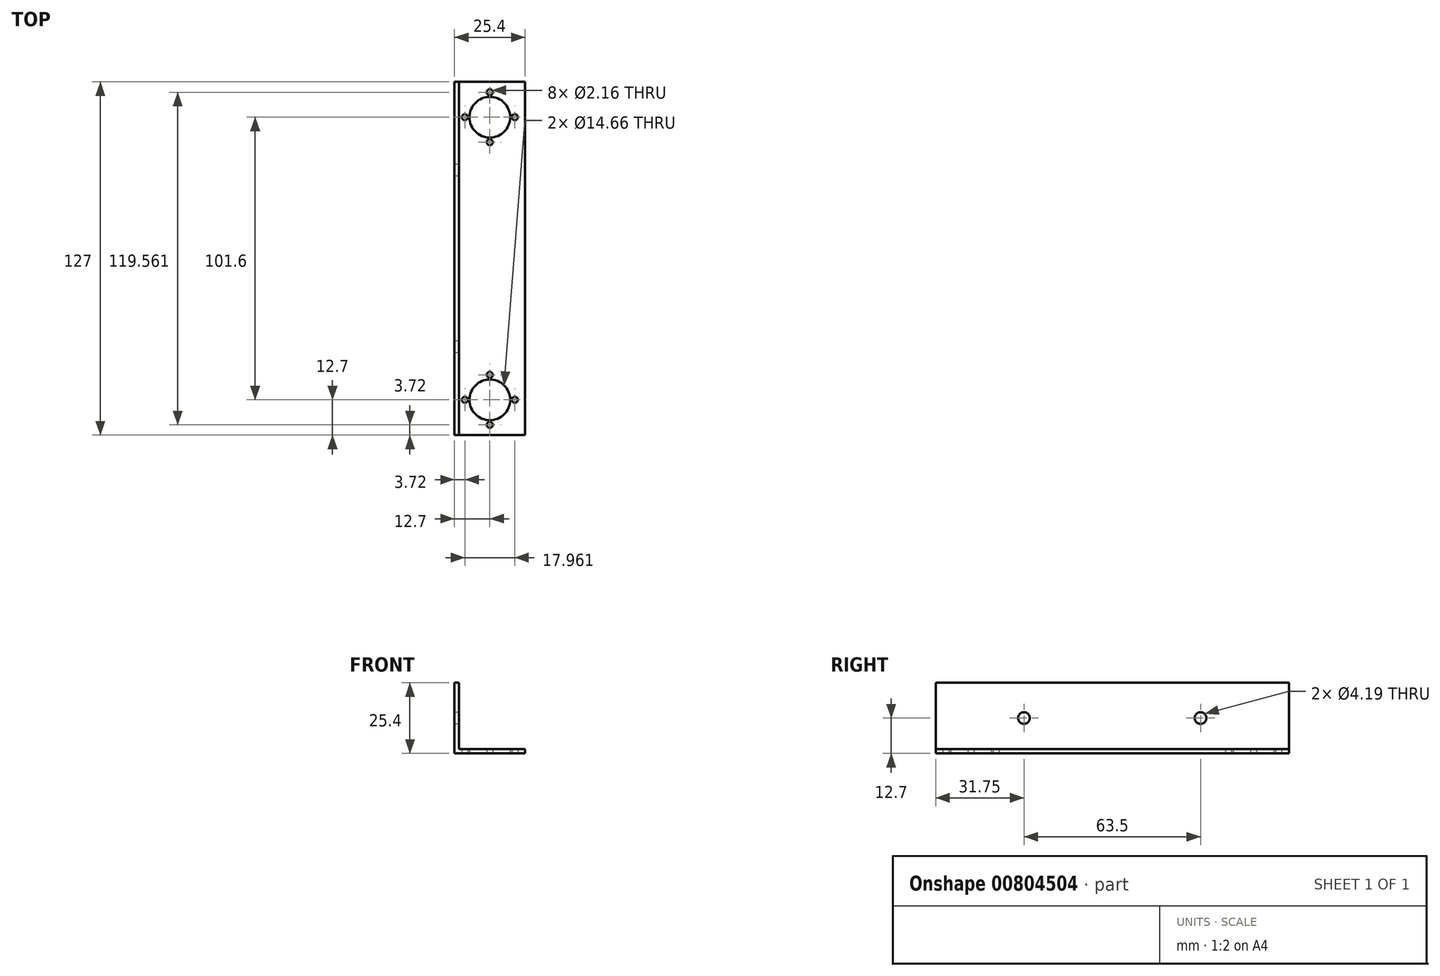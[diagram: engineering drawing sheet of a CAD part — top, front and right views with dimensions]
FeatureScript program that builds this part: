
annotation { "Feature Type Name" : "Feature", "Feature Type Description" : "" }
export const myFeature = defineFeature(function(context is Context, id is Id, definition is map)
    precondition{}
    {
        {
            var Q0;
            Q0=qCreatedBy(makeId("Top.planeOp"),FACE);
            var sketch = newSketch(context, id + "F0", { "sketchPlane" : qUnion([Q0])});
            skLineSegment(sketch, "E0", {"start": v(0, 0) * mm, "end": v(19.87, 0) * mm, "construction": true});
            skCircle(sketch, "E1", {"center": v(0, 50.8) * mm, "radius": 7.33 * mm});
            skLineSegment(sketch, "E2", {"start": v(0, 59.78) * mm, "end": v(0, 41.82) * mm, "construction": true});
            skLineSegment(sketch, "E3", {"start": v(-8.98, 50.8) * mm, "end": v(8.98, 50.8) * mm, "construction": true});
            skCircle(sketch, "E4", {"center": v(0, 59.78) * mm, "radius": 1.08 * mm});
            skCircle(sketch, "E5", {"center": v(8.98, 50.8) * mm, "radius": 1.08 * mm});
            skCircle(sketch, "E6", {"center": v(0, 41.82) * mm, "radius": 1.08 * mm});
            skCircle(sketch, "E7", {"center": v(-8.98, 50.8) * mm, "radius": 1.08 * mm});
            skSolve(sketch);
        }
        {
            var Q0;
            Q0=qCreatedBy(makeId("Front.planeOp"),FACE);
            var sketch = newSketch(context, id + "F1", { "sketchPlane" : qUnion([Q0])});
            skLineSegment(sketch, "E8", {"start": v(12.7, 1.59) * mm, "end": v(-11.11, 1.59) * mm});
            skLineSegment(sketch, "E9", {"start": v(-11.11, 1.59) * mm, "end": v(-11.11, 25.4) * mm});
            skLineSegment(sketch, "E10", {"start": v(-11.11, 25.4) * mm, "end": v(-12.7, 25.4) * mm});
            skLineSegment(sketch, "E11", {"start": v(-12.7, 25.4) * mm, "end": v(-12.7, 0) * mm});
            skLineSegment(sketch, "E12", {"start": v(-12.7, 0) * mm, "end": v(12.7, 0) * mm});
            skLineSegment(sketch, "E13", {"start": v(12.7, 0) * mm, "end": v(12.7, 1.59) * mm});
            skSolve(sketch);
        }
        {
            var Q0;
            Q0=makeQuery(id+"F1.imprint","IMPRINT",FACE,{"disambiguationData":[TD([[makeQuery(id+"F1.imprint","IMPRINT",EDGE,{"derivedFrom":sQuery(id+"F1.wireOp",EDGE,"E8")}),1.0]])]});
            extrude(context, id + "F2", {"entities" : qUnion([Q0]), "endBound" : BoundingType.SYMMETRIC, "depth" : 127 * mm, "offsetDistance" : 25.4 * mm});
        }
        {
            var Q0;
            Q0=makeQuery(id+"F0.imprint","IMPRINT",FACE,{"disambiguationData":[TD([[makeQuery(id+"F0.imprint","IMPRINT",EDGE,{"derivedFrom":sQuery(id+"F0.wireOp",EDGE,"E1")}),1.0]])]});
            var Q1;
            Q1=makeQuery(id+"F0.imprint","IMPRINT",FACE,{"disambiguationData":[TD([[makeQuery(id+"F0.imprint","IMPRINT",EDGE,{"derivedFrom":sQuery(id+"F0.wireOp",EDGE,"E4")}),1.0]])]});
            var Q2;
            Q2=makeQuery(id+"F0.imprint","IMPRINT",FACE,{"disambiguationData":[TD([[makeQuery(id+"F0.imprint","IMPRINT",EDGE,{"derivedFrom":sQuery(id+"F0.wireOp",EDGE,"E5")}),1.0]])]});
            var Q3;
            Q3=makeQuery(id+"F0.imprint","IMPRINT",FACE,{"disambiguationData":[TD([[makeQuery(id+"F0.imprint","IMPRINT",EDGE,{"derivedFrom":sQuery(id+"F0.wireOp",EDGE,"E6")}),1.0]])]});
            var Q4;
            Q4=makeQuery(id+"F0.imprint","IMPRINT",FACE,{"disambiguationData":[TD([[makeQuery(id+"F0.imprint","IMPRINT",EDGE,{"derivedFrom":sQuery(id+"F0.wireOp",EDGE,"E7")}),1.0]])]});
            extrude(context, id + "F3", {"entities" : qUnion([Q0, Q1, Q2, Q3, Q4]), "endBound" : BoundingType.THROUGH_ALL, "depth" : 25.4 * mm, "offsetDistance" : 25.4 * mm});
        }
        {
            var Q0;
            Q0=makeQuery(id+"F2.opExtrude","SWEPT_FACE",FACE,{"disambiguationData":[OSD([sQuery(id+"F1.wireOp",EDGE,"E11")])]});
            var sketch = newSketch(context, id + "F4", { "sketchPlane" : qUnion([Q0])});
            skLineSegment(sketch, "E14", {"start": v(0, 0) * mm, "end": v(0, 25.4) * mm, "construction": true});
            skCircle(sketch, "E15", {"center": v(-31.75, 12.7) * mm, "radius": 2.1 * mm});
            skPoint(sketch, "E15.centerSnap0", {"position": v(0, 12.7) * mm});
            skSolve(sketch);
        }
        {
            var Q0;
            Q0=qSketchRegion(id+"F4",true);
            extrude(context, id + "F5", {"entities" : qUnion([Q0]), "endBound" : BoundingType.THROUGH_ALL, "oppositeDirection" : true, "depth" : 25.4 * mm, "offsetDistance" : 25.4 * mm});
        }
        {
            var Q0;
            Q0=makeQuery(id+"F3.opExtrude","SWEPT_BODY",BODY,{"disambiguationData":[OSD([sQuery(id+"F0.wireOp",EDGE,"E1")])]});
            var Q1;
            Q1=makeQuery(id+"F3.opExtrude","SWEPT_BODY",BODY,{"disambiguationData":[OSD([sQuery(id+"F0.wireOp",EDGE,"E4")])]});
            var Q2;
            Q2=makeQuery(id+"F3.opExtrude","SWEPT_BODY",BODY,{"disambiguationData":[OSD([sQuery(id+"F0.wireOp",EDGE,"E5")])]});
            var Q3;
            Q3=makeQuery(id+"F3.opExtrude","SWEPT_BODY",BODY,{"disambiguationData":[OSD([sQuery(id+"F0.wireOp",EDGE,"E6")])]});
            var Q4;
            Q4=makeQuery(id+"F3.opExtrude","SWEPT_BODY",BODY,{"disambiguationData":[OSD([sQuery(id+"F0.wireOp",EDGE,"E7")])]});
            var Q5;
            Q5=makeQuery(id+"F5.opExtrude","SWEPT_BODY",BODY,{"disambiguationData":[OSD([sQuery(id+"F4.wireOp",EDGE,"E15")])]});
            var Q6;
            Q6=qCreatedBy(makeId("Front.planeOp"),FACE);
            mirror(context, id + "F6", {"entities" : qUnion([Q0, Q1, Q2, Q3, Q4, Q5]), "mirrorPlane" : qUnion([Q6])});
        }
        {
            var Q0;
            Q0=makeQuery(id+"F5.opExtrude","SWEPT_BODY",BODY,{"disambiguationData":[OSD([sQuery(id+"F4.wireOp",EDGE,"E15")])]});
            var Q1;
            Q1=makeQuery(id+"F6.opPattern","COPY",BODY,{"derivedFrom":makeQuery(id+"F5.opExtrude","SWEPT_BODY",BODY,{"disambiguationData":[OSD([sQuery(id+"F4.wireOp",EDGE,"E15")])]}),"instanceName":"1"});
            var Q2;
            Q2=makeQuery(id+"F3.opExtrude","SWEPT_BODY",BODY,{"disambiguationData":[OSD([sQuery(id+"F0.wireOp",EDGE,"E5")])]});
            var Q3;
            Q3=makeQuery(id+"F3.opExtrude","SWEPT_BODY",BODY,{"disambiguationData":[OSD([sQuery(id+"F0.wireOp",EDGE,"E1")])]});
            var Q4;
            Q4=makeQuery(id+"F3.opExtrude","SWEPT_BODY",BODY,{"disambiguationData":[OSD([sQuery(id+"F0.wireOp",EDGE,"E6")])]});
            var Q5;
            Q5=makeQuery(id+"F3.opExtrude","SWEPT_BODY",BODY,{"disambiguationData":[OSD([sQuery(id+"F0.wireOp",EDGE,"E4")])]});
            var Q6;
            Q6=makeQuery(id+"F3.opExtrude","SWEPT_BODY",BODY,{"disambiguationData":[OSD([sQuery(id+"F0.wireOp",EDGE,"E7")])]});
            var Q7;
            Q7=makeQuery(id+"F6.opPattern","COPY",BODY,{"derivedFrom":makeQuery(id+"F3.opExtrude","SWEPT_BODY",BODY,{"disambiguationData":[OSD([sQuery(id+"F0.wireOp",EDGE,"E5")])]}),"instanceName":"1"});
            var Q8;
            Q8=makeQuery(id+"F6.opPattern","COPY",BODY,{"derivedFrom":makeQuery(id+"F3.opExtrude","SWEPT_BODY",BODY,{"disambiguationData":[OSD([sQuery(id+"F0.wireOp",EDGE,"E4")])]}),"instanceName":"1"});
            var Q9;
            Q9=makeQuery(id+"F6.opPattern","COPY",BODY,{"derivedFrom":makeQuery(id+"F3.opExtrude","SWEPT_BODY",BODY,{"disambiguationData":[OSD([sQuery(id+"F0.wireOp",EDGE,"E1")])]}),"instanceName":"1"});
            var Q10;
            Q10=makeQuery(id+"F6.opPattern","COPY",BODY,{"derivedFrom":makeQuery(id+"F3.opExtrude","SWEPT_BODY",BODY,{"disambiguationData":[OSD([sQuery(id+"F0.wireOp",EDGE,"E7")])]}),"instanceName":"1"});
            var Q11;
            Q11=makeQuery(id+"F6.opPattern","COPY",BODY,{"derivedFrom":makeQuery(id+"F3.opExtrude","SWEPT_BODY",BODY,{"disambiguationData":[OSD([sQuery(id+"F0.wireOp",EDGE,"E6")])]}),"instanceName":"1"});
            var Q12;
            Q12=makeQuery(id+"F2.opExtrude","SWEPT_BODY",BODY,{"disambiguationData":[OSD([sQuery(id+"F1.wireOp",EDGE,"E8"),sQuery(id+"F1.wireOp",EDGE,"E9"),sQuery(id+"F1.wireOp",EDGE,"E10"),sQuery(id+"F1.wireOp",EDGE,"E11"),sQuery(id+"F1.wireOp",EDGE,"E12"),sQuery(id+"F1.wireOp",EDGE,"E13")])]});
            booleanBodies(context, id + "F7", {"operationType" : BooleanOperationType.SUBTRACTION, "tools" : qUnion([Q0, Q1, Q2, Q3, Q4, Q5, Q6, Q7, Q8, Q9, Q10, Q11]), "targets" : qUnion([Q12])});
        }
    });
